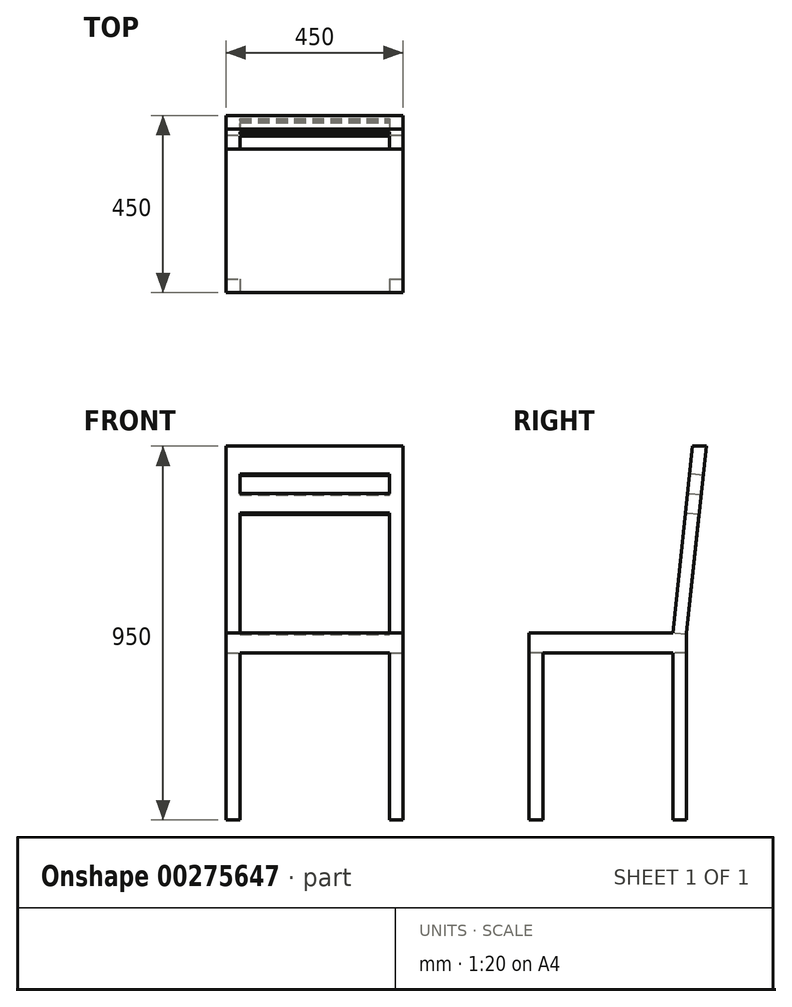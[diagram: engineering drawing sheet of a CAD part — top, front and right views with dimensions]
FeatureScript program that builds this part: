
annotation { "Feature Type Name" : "Feature", "Feature Type Description" : "" }
export const myFeature = defineFeature(function(context is Context, id is Id, definition is map)
    precondition{}
    {
        {
            var Q0;
            Q0=qCreatedBy(makeId("Top.planeOp"),FACE);
            var sketch = newSketch(context, id + "F0", { "sketchPlane" : qUnion([Q0])});
            skLineSegment(sketch, "E0.bottom", {"start": v(225, 225) * mm, "end": v(-225, 225) * mm});
            skLineSegment(sketch, "E0.top", {"start": v(225, -225) * mm, "end": v(-225, -225) * mm});
            skLineSegment(sketch, "E0.left", {"start": v(225, 225) * mm, "end": v(225, -225) * mm});
            skLineSegment(sketch, "E0.right", {"start": v(-225, 225) * mm, "end": v(-225, -225) * mm});
            skPoint(sketch, "E0.middle", {"position": v(0, 0) * mm});
            skSolve(sketch);
        }
        {
            var Q0;
            Q0=qSketchRegion(id+"F0",true);
            extrude(context, id + "F1", {"entities" : qUnion([Q0]), "depth" : 950 * mm});
        }
        {
            var Q0;
            Q0=makeQuery(id+"F1.opExtrude","SWEPT_FACE",FACE,{"disambiguationData":[OSD([sQuery(id+"F0.wireOp",EDGE,"E0.left")])]});
            var sketch = newSketch(context, id + "F2", { "sketchPlane" : qUnion([Q0])});
            skLineSegment(sketch, "E1.bottom", {"start": v(225, 475) * mm, "end": v(-225, 475) * mm});
            skLineSegment(sketch, "E1.top", {"start": v(225, 425) * mm, "end": v(-225, 425) * mm});
            skLineSegment(sketch, "E1.left", {"start": v(225, 475) * mm, "end": v(225, 425) * mm});
            skLineSegment(sketch, "E1.right", {"start": v(-225, 475) * mm, "end": v(-225, 425) * mm});
            skLineSegment(sketch, "E2", {"start": v(225, 950) * mm, "end": v(175, 475) * mm});
            skLineSegment(sketch, "E3", {"start": v(190, 950) * mm, "end": v(140, 475) * mm});
            skLineSegment(sketch, "E4", {"start": v(175, 475) * mm, "end": v(175, 0) * mm});
            skLineSegment(sketch, "E5", {"start": v(140, 475) * mm, "end": v(140, 0) * mm});
            skLineSegment(sketch, "E6.bottom", {"start": v(-225, 0) * mm, "end": v(-190, 0) * mm});
            skLineSegment(sketch, "E6.top", {"start": v(-225, 425) * mm, "end": v(-190, 425) * mm});
            skLineSegment(sketch, "E6.left", {"start": v(-225, 0) * mm, "end": v(-225, 425) * mm});
            skLineSegment(sketch, "E6.right", {"start": v(-190, 0) * mm, "end": v(-190, 425) * mm});
            skSolve(sketch);
        }
        {
            var Q0;
            {var subQ4=sQuery(id+"F2.wireOp",EDGE,"E3");Q0=makeQuery(id+"F2.imprint","IMPRINT",FACE,{"disambiguationData":[TD([[makeQuery(id+"F2.imprint","IMPRINT",EDGE,{"derivedFrom":subQ4}),-1.0]])]});}
            var Q1;
            {var subQ4=sQuery(id+"F2.wireOp",EDGE,"E2");Q1=makeQuery(id+"F2.imprint","IMPRINT",FACE,{"disambiguationData":[TD([[makeQuery(id+"F2.imprint","IMPRINT",EDGE,{"derivedFrom":subQ4}),1.0]])]});}
            var Q2;
            {var subQ0=sQuery(id+"F2.wireOp",EDGE,"E1.left");Q2=makeQuery(id+"F2.imprint","IMPRINT",FACE,{"disambiguationData":[TD([[makeQuery(id+"F2.imprint","IMPRINT",EDGE,{"derivedFrom":subQ0}),-1.0]])]});}
            var Q3;
            {var subQ1=sQuery(id+"F0.wireOp",EDGE,"E0.left");var subQ4=sQuery(id+"F2.wireOp",EDGE,"E4");var subQ6=makeQuery(id+"F1.opExtrude","CAP_EDGE",EDGE,{"disambiguationData":[OSD([subQ1])],"isStart":true});var subQ7=makeQuery(id+"F2.imprint","INTERSECT",VERTEX,{"derivedFrom":[subQ6,subQ4]});Q3=makeQuery(id+"F2.imprint","IMPRINT",FACE,{"disambiguationData":[TD([[makeQuery(id+"F2.imprint","IMPRINT",EDGE,{"disambiguationData":[TD([[subQ7,1.0]])],"derivedFrom":subQ4}),1.0]])]});}
            var Q4;
            {var subQ0=sQuery(id+"F2.wireOp",EDGE,"E6.right");Q4=makeQuery(id+"F2.imprint","IMPRINT",FACE,{"disambiguationData":[TD([[makeQuery(id+"F2.imprint","IMPRINT",EDGE,{"derivedFrom":subQ0}),-1.0]])]});}
            extrude(context, id + "F3", {"entities" : qUnion([Q0, Q1, Q2, Q3, Q4]), "operationType" : NewBodyOperationType.REMOVE, "endBound" : BoundingType.THROUGH_ALL, "oppositeDirection" : true, "depth" : 25 * mm});
        }
        {
            var Q0;
            Q0=makeQuery(id+"F1.opExtrude","SWEPT_FACE",FACE,{"disambiguationData":[OSD([sQuery(id+"F0.wireOp",EDGE,"E0.top")])]});
            var sketch = newSketch(context, id + "F4", { "sketchPlane" : qUnion([Q0])});
            skLineSegment(sketch, "E7", {"start": v(-190, 0) * mm, "end": v(-190, 425) * mm});
            skLineSegment(sketch, "E8", {"start": v(-190, 425) * mm, "end": v(190, 425) * mm});
            skLineSegment(sketch, "E9", {"start": v(190, 425) * mm, "end": v(190, 0) * mm});
            skSolve(sketch);
        }
        {
            var Q0;
            {var subQ0=sQuery(id+"F4.wireOp",EDGE,"E7");Q0=makeQuery(id+"F4.imprint","IMPRINT",FACE,{"disambiguationData":[TD([[makeQuery(id+"F4.imprint","IMPRINT",EDGE,{"derivedFrom":subQ0}),-1.0]])]});}
            extrude(context, id + "F5", {"entities" : qUnion([Q0]), "operationType" : NewBodyOperationType.REMOVE, "endBound" : BoundingType.THROUGH_ALL, "oppositeDirection" : true, "depth" : 25 * mm});
        }
        {
            var Q0;
            Q0=makeQuery(id+"F3.boolean.opBoolean","COPY",FACE,{"derivedFrom":makeQuery(id+"F3.opExtrude","SWEPT_FACE",FACE,{"disambiguationData":[OSD([sQuery(id+"F2.wireOp",EDGE,"E3")])]})});
            var sketch = newSketch(context, id + "F6", { "sketchPlane" : qUnion([Q0])});
            skLineSegment(sketch, "E10", {"start": v(-190, 487.05) * mm, "end": v(-190, 893.33) * mm});
            skLineSegment(sketch, "E11", {"start": v(-190, 893.33) * mm, "end": v(190, 893.33) * mm});
            skLineSegment(sketch, "E12", {"start": v(190, 893.33) * mm, "end": v(190, 487.05) * mm});
            skLineSegment(sketch, "E13", {"start": v(-190, 843.33) * mm, "end": v(190, 843.33) * mm});
            skLineSegment(sketch, "E14", {"start": v(-190, 793.33) * mm, "end": v(190, 793.33) * mm});
            skSolve(sketch);
        }
        {
            var Q0;
            {var subQ0=sQuery(id+"F6.wireOp",EDGE,"E11");Q0=makeQuery(id+"F6.imprint","IMPRINT",FACE,{"disambiguationData":[TD([[makeQuery(id+"F6.imprint","IMPRINT",EDGE,{"derivedFrom":subQ0}),-1.0]])]});}
            var Q1;
            {var subQ3=sQuery(id+"F6.wireOp",EDGE,"E14");Q1=makeQuery(id+"F6.imprint","IMPRINT",FACE,{"disambiguationData":[TD([[makeQuery(id+"F6.imprint","IMPRINT",EDGE,{"derivedFrom":subQ3}),-1.0]])]});}
            extrude(context, id + "F7", {"entities" : qUnion([Q0, Q1]), "operationType" : NewBodyOperationType.REMOVE, "endBound" : BoundingType.THROUGH_ALL, "oppositeDirection" : true, "depth" : 25 * mm});
        }
    });
